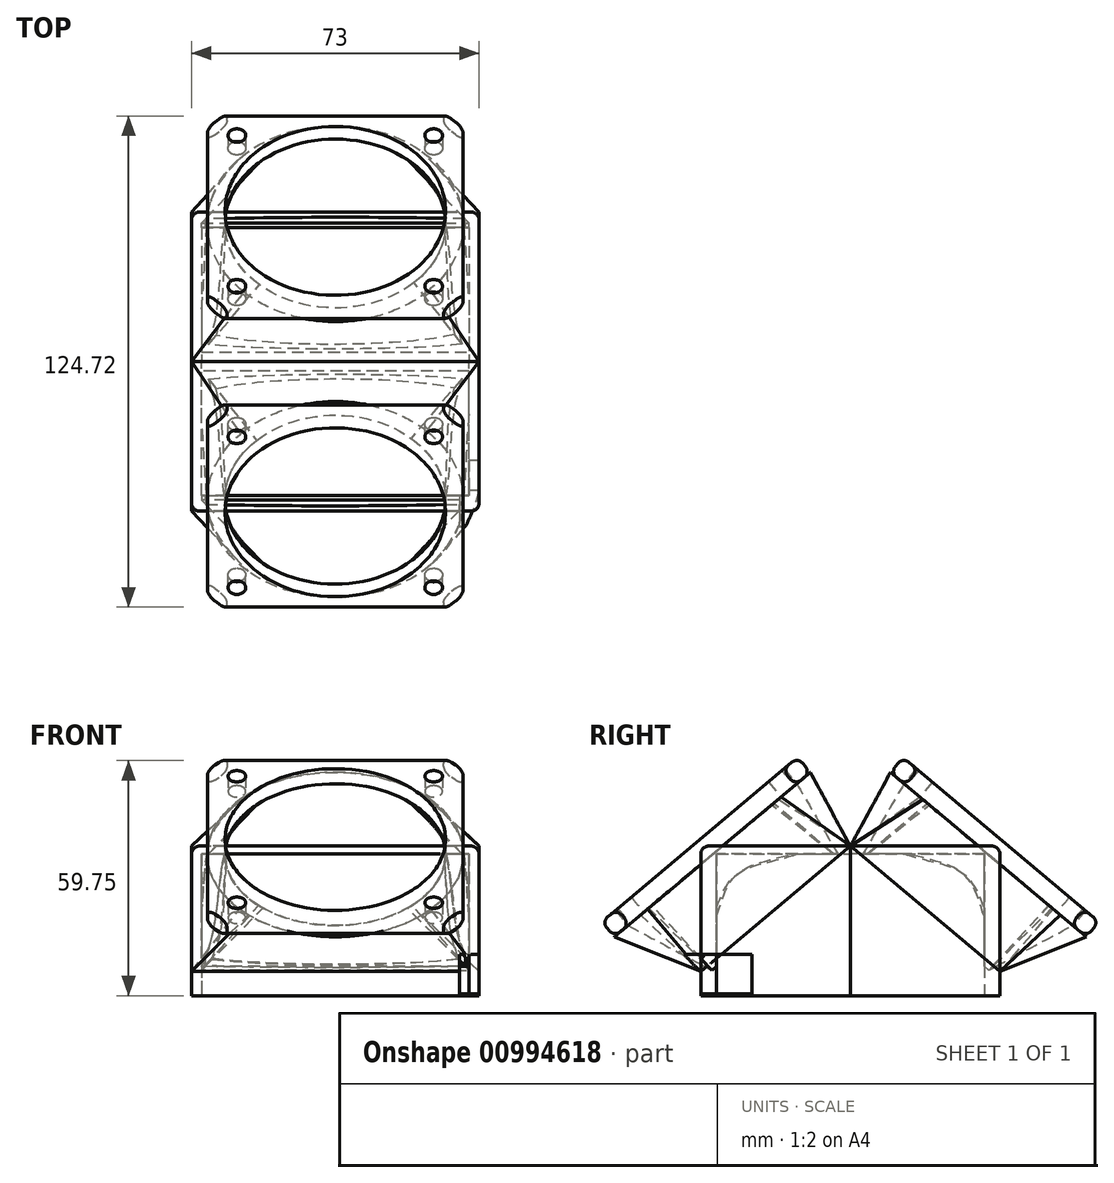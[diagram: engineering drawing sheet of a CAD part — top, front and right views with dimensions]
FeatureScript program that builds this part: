
annotation { "Feature Type Name" : "Feature", "Feature Type Description" : "" }
export const myFeature = defineFeature(function(context is Context, id is Id, definition is map)
    precondition{}
    {
        {
            var Q0;
            Q0=qCreatedBy(makeId("Front.planeOp"),FACE);
            var sketch = newSketch(context, id + "F0", { "sketchPlane" : qUnion([Q0])});
            skLineSegment(sketch, "E0.bottom", {"start": v(-34, 18) * mm, "end": v(34, 18) * mm});
            skLineSegment(sketch, "E0.top", {"start": v(-34, -18) * mm, "end": v(34, -18) * mm});
            skLineSegment(sketch, "E0.left", {"start": v(-34, 18) * mm, "end": v(-34, -18) * mm});
            skLineSegment(sketch, "E0.right", {"start": v(34, 18) * mm, "end": v(34, -18) * mm});
            skPoint(sketch, "E0.middle", {"position": v(0, 0) * mm});
            skSolve(sketch);
        }
        {
            var Q0;
            Q0=makeQuery(id+"F0.imprint","IMPRINT",FACE,{"disambiguationData":[TD([[makeQuery(id+"F0.imprint","IMPRINT",EDGE,{"derivedFrom":sQuery(id+"F0.wireOp",EDGE,"E0.bottom")}),-1.0]])]});
            extrude(context, id + "F1", {"entities" : qUnion([Q0]), "depth" : 34 * mm, "offsetDistance" : 25 * mm});
        }
        {
            var Q0;
            Q0=makeQuery(id+"F0.imprint","IMPRINT",FACE,{"disambiguationData":[TD([[makeQuery(id+"F0.imprint","IMPRINT",EDGE,{"derivedFrom":sQuery(id+"F0.wireOp",EDGE,"E0.bottom")}),-1.0]])]});
            var sketch = newSketch(context, id + "F2", { "sketchPlane" : qUnion([Q0])});
            skLineSegment(sketch, "E1", {"start": v(0, 18) * mm, "end": v(0, -18) * mm, "construction": true});
            skSolve(sketch);
        }
        {
            var Q0;
            Q0=sQuery(id+"F0.wireOp",EDGE,"E0.top");
            cPlane(context, id + "F3", {"entities" : qUnion([Q0]), "cplaneType" : CPlaneType.LINE_ANGLE, "offset" : 25 * mm, "angle" : 50 * degree, "oppositeDirection" : true, "width" : 150 * mm, "height" : 150 * mm});
        }
        {
            var Q0;
            Q0=sQuery(id+"F0.wireOp",EDGE,"E0.bottom");
            var Q1;
            Q1=qBodyType(qCreatedBy(id+"F5",EDGE),BodyType.WIRE);
            cPlane(context, id + "F4", {"entities" : qUnion([Q0, Q1]), "cplaneType" : CPlaneType.LINE_ANGLE, "offset" : 25 * mm, "angle" : 50 * degree, "oppositeDirection" : true, "width" : 150 * mm, "height" : 150 * mm});
        }
        {
            var Q0;
            Q0=qCreatedBy(id+"F4.planeOp",FACE);
            var sketch = newSketch(context, id + "F5", { "sketchPlane" : qUnion([Q0])});
            skLineSegment(sketch, "E2.bottom", {"start": v(34, -8.77) * mm, "end": v(-34, -8.77) * mm});
            skLineSegment(sketch, "E2.top", {"start": v(34, 34.4) * mm, "end": v(-34, 34.4) * mm});
            skLineSegment(sketch, "E2.left", {"start": v(34, -8.77) * mm, "end": v(34, 34.4) * mm});
            skLineSegment(sketch, "E2.right", {"start": v(-34, -8.77) * mm, "end": v(-34, 34.4) * mm});
            skSolve(sketch);
        }
        {
            var Q0;
            Q0=qCreatedBy(id+"F3.planeOp",FACE);
            cPlane(context, id + "F6", {"entities" : qUnion([Q0]), "cplaneType" : CPlaneType.OFFSET, "offset" : 50 * mm, "oppositeDirection" : true, "width" : 150 * mm, "height" : 150 * mm});
        }
        {
            var Q0;
            Q0=qCreatedBy(id+"F6.planeOp",FACE);
            var sketch = newSketch(context, id + "F7", { "sketchPlane" : qUnion([Q0])});
            skArc(sketch, "E3", {"start": v(19.5, 35.49) * mm, "mid": v(0.77, 43.38) * mm, "end": v(-18.36, 36.53) * mm});
            skArc(sketch, "E4", {"start": v(-18.36, 36.53) * mm, "mid": v(-27.98, 16.5) * mm, "end": v(-19.97, -4.24) * mm});
            skArc(sketch, "E5", {"start": v(-19.97, -4.24) * mm, "mid": v(-0.48, -12.6) * mm, "end": v(19.28, -4.91) * mm});
            skArc(sketch, "E6", {"start": v(19.28, -4.91) * mm, "mid": v(28, 15.24) * mm, "end": v(19.5, 35.49) * mm});
            skSolve(sketch);
        }
        {
            var Q0;
            Q0=qSketchRegion(id+"F5",true);
            var Q1;
            Q1=makeQuery(id+"F7.imprint","IMPRINT",FACE,{"disambiguationData":[TD([[makeQuery(id+"F7.imprint","IMPRINT",EDGE,{"derivedFrom":sQuery(id+"F7.wireOp",EDGE,"E3")}),1.0]])]});
            loft(context, id + "F8", {"sheetProfilesArray" : [{ "sheetProfileEntities" : qUnion([Q0]) }, { "sheetProfileEntities" : qUnion([Q1]) }]});
        }
        {
            var Q0;
            Q0=makeQuery(id+"F2.imprint","IMPRINT",FACE,{"disambiguationData":[TD([[makeQuery(id+"F2.imprint","IMPRINT",EDGE,{"derivedFrom":makeQuery(id+"F0.imprint","IMPRINT",EDGE,{"derivedFrom":sQuery(id+"F0.wireOp",EDGE,"E0.bottom")})}),-1.0]])]});
            var sketch = newSketch(context, id + "F9", { "sketchPlane" : qUnion([Q0])});
            skLineSegment(sketch, "E7.bottom", {"start": v(36.5, 20) * mm, "end": v(-36.5, 20) * mm});
            skLineSegment(sketch, "E7.top", {"start": v(36.5, -18) * mm, "end": v(-36.5, -18) * mm});
            skLineSegment(sketch, "E7.left", {"start": v(36.5, 20) * mm, "end": v(36.5, -18) * mm});
            skLineSegment(sketch, "E7.right", {"start": v(-36.5, 20) * mm, "end": v(-36.5, -18) * mm});
            skPoint(sketch, "E7.middle", {"position": v(0, 0) * mm});
            skSolve(sketch);
        }
        {
            var Q0;
            Q0=qSketchRegion(id+"F9",true);
            extrude(context, id + "F10", {"entities" : qUnion([Q0]), "depth" : 38 * mm, "offsetDistance" : 25 * mm});
        }
        {
            var Q0;
            Q0=sQuery(id+"F9.wireOp",EDGE,"E7.bottom");
            cPlane(context, id + "F11", {"entities" : qUnion([Q0]), "cplaneType" : CPlaneType.LINE_ANGLE, "offset" : 25 * mm, "angle" : 50 * degree, "width" : 150 * mm, "height" : 150 * mm});
        }
        {
            var Q0;
            Q0=qCreatedBy(id+"F11.planeOp",FACE);
            var sketch = newSketch(context, id + "F12", { "sketchPlane" : qUnion([Q0])});
            skLineSegment(sketch, "E8.bottom", {"start": v(-36.5, 12.86) * mm, "end": v(36.5, 12.86) * mm});
            skLineSegment(sketch, "E8.top", {"start": v(-36.5, -36.75) * mm, "end": v(36.5, -36.75) * mm});
            skLineSegment(sketch, "E8.left", {"start": v(-36.5, 12.86) * mm, "end": v(-36.5, -36.75) * mm});
            skLineSegment(sketch, "E8.right", {"start": v(36.5, 12.86) * mm, "end": v(36.5, -36.75) * mm});
            skSolve(sketch);
        }
        {
            var Q0;
            Q0=qCreatedBy(id+"F6.planeOp",FACE);
            var sketch = newSketch(context, id + "F13", { "sketchPlane" : qUnion([Q0])});
            skArc(sketch, "E9", {"start": v(-24.1, -6.4) * mm, "mid": v(-0.67, -17.1) * mm, "end": v(23.2, -7.38) * mm});
            skArc(sketch, "E10", {"start": v(-22.1, 39.22) * mm, "mid": v(-32.47, 16.82) * mm, "end": v(-24.1, -6.4) * mm});
            skArc(sketch, "E11", {"start": v(24.32, 36.95) * mm, "mid": v(1.59, 47.85) * mm, "end": v(-22.1, 39.22) * mm});
            skArc(sketch, "E12", {"start": v(23.2, -7.38) * mm, "mid": v(32.49, 14.56) * mm, "end": v(24.32, 36.95) * mm});
            skSolve(sketch);
        }
        {
            var Q0;
            Q0=qCreatedBy(id+"F6.planeOp",FACE);
            var sketch = newSketch(context, id + "F14", { "sketchPlane" : qUnion([Q0])});
            skLineSegment(sketch, "E13.bottom", {"start": v(-32.5, -17.1) * mm, "end": v(32.5, -17.1) * mm});
            skLineSegment(sketch, "E13.top", {"start": v(-32.5, 47.9) * mm, "end": v(32.5, 47.9) * mm});
            skLineSegment(sketch, "E13.left", {"start": v(-32.5, -17.1) * mm, "end": v(-32.5, 47.9) * mm});
            skLineSegment(sketch, "E13.right", {"start": v(32.5, -17.1) * mm, "end": v(32.5, 47.9) * mm});
            skPoint(sketch, "E13.middle", {"position": v(0, 15.4) * mm});
            skSolve(sketch);
        }
        {
            var Q0;
            Q0=qCreatedBy(id+"F6.planeOp",FACE);
            var sketch = newSketch(context, id + "F15", { "sketchPlane" : qUnion([Q0])});
            skLineSegment(sketch, "E14.bottom", {"start": v(-25, -9.6) * mm, "end": v(25, -9.6) * mm, "construction": true});
            skLineSegment(sketch, "E14.top", {"start": v(-25, 40.4) * mm, "end": v(25, 40.4) * mm, "construction": true});
            skLineSegment(sketch, "E14.left", {"start": v(-25, -9.6) * mm, "end": v(-25, 40.4) * mm, "construction": true});
            skLineSegment(sketch, "E14.right", {"start": v(25, -9.6) * mm, "end": v(25, 40.4) * mm, "construction": true});
            skPoint(sketch, "E14.middle", {"position": v(0, 15.4) * mm});
            skSolve(sketch);
        }
        {
            var Q0;
            Q0=qCreatedBy(id+"F6.planeOp",FACE);
            var sketch = newSketch(context, id + "F16", { "sketchPlane" : qUnion([Q0])});
            skCircle(sketch, "E15", {"center": v(25, -9.6) * mm, "radius": 2.25 * mm});
            skCircle(sketch, "E16", {"center": v(-25, -9.6) * mm, "radius": 2.25 * mm});
            skCircle(sketch, "E17", {"center": v(-25, 40.4) * mm, "radius": 2.25 * mm});
            skCircle(sketch, "E18", {"center": v(25, 40.4) * mm, "radius": 2.25 * mm});
            skSolve(sketch);
        }
        {
            var Q0;
            Q0=makeQuery(id+"F8.opLoft","CAP_FACE",FACE,{"disambiguationData":[OSD([makeQuery(id+"F7.imprint","IMPRINT",FACE,{"disambiguationData":[TD([[makeQuery(id+"F7.imprint","IMPRINT",EDGE,{"derivedFrom":sQuery(id+"F7.wireOp",EDGE,"E3")}),1.0]])]})])],"isStart":true});
            var Q1;
            Q1=makeQuery(id+"F16.imprint","IMPRINT",FACE,{"disambiguationData":[TD([[makeQuery(id+"F16.imprint","IMPRINT",EDGE,{"derivedFrom":sQuery(id+"F16.wireOp",EDGE,"E18")}),1.0]])]});
            var Q2;
            Q2=makeQuery(id+"F16.imprint","IMPRINT",FACE,{"disambiguationData":[TD([[makeQuery(id+"F16.imprint","IMPRINT",EDGE,{"derivedFrom":sQuery(id+"F16.wireOp",EDGE,"E17")}),1.0]])]});
            var Q3;
            Q3=makeQuery(id+"F16.imprint","IMPRINT",FACE,{"disambiguationData":[TD([[makeQuery(id+"F16.imprint","IMPRINT",EDGE,{"derivedFrom":sQuery(id+"F16.wireOp",EDGE,"E16")}),1.0]])]});
            var Q4;
            Q4=makeQuery(id+"F16.imprint","IMPRINT",FACE,{"disambiguationData":[TD([[makeQuery(id+"F16.imprint","IMPRINT",EDGE,{"derivedFrom":sQuery(id+"F16.wireOp",EDGE,"E15")}),1.0]])]});
            extrude(context, id + "F17", {"entities" : qUnion([Q0, Q1, Q2, Q3, Q4]), "depth" : 5 * mm, "offsetDistance" : 25 * mm});
        }
        {
            var Q0;
            Q0=makeQuery(id+"F12.imprint","IMPRINT",FACE,{"disambiguationData":[TD([[makeQuery(id+"F12.imprint","IMPRINT",EDGE,{"derivedFrom":sQuery(id+"F12.wireOp",EDGE,"E8.bottom")}),-1.0]])]});
            var Q1;
            Q1=qSketchRegion(id+"F13",true);
            loft(context, id + "F18", {"sheetProfilesArray" : [{ "sheetProfileEntities" : qUnion([Q0]) }, { "sheetProfileEntities" : qUnion([Q1]) }]});
        }
        {
            var Q0;
            Q0=makeQuery(id+"F14.imprint","IMPRINT",FACE,{"disambiguationData":[TD([[makeQuery(id+"F14.imprint","IMPRINT",EDGE,{"derivedFrom":sQuery(id+"F14.wireOp",EDGE,"E13.bottom")}),1.0]])]});
            extrude(context, id + "F19", {"entities" : qUnion([Q0]), "oppositeDirection" : true, "depth" : 5 * mm, "offsetDistance" : 25 * mm});
        }
        {
            var Q0;
            Q0=makeQuery(id+"F17.opExtrude","SWEPT_BODY",BODY,{"disambiguationData":[OSD([sQuery(id+"F16.wireOp",EDGE,"E18")])]});
            var Q1;
            Q1=makeQuery(id+"F17.opExtrude","SWEPT_BODY",BODY,{"disambiguationData":[OSD([sQuery(id+"F16.wireOp",EDGE,"E17")])]});
            var Q2;
            Q2=makeQuery(id+"F17.opExtrude","SWEPT_BODY",BODY,{"disambiguationData":[OSD([sQuery(id+"F16.wireOp",EDGE,"E16")])]});
            var Q3;
            Q3=makeQuery(id+"F17.opExtrude","SWEPT_BODY",BODY,{"disambiguationData":[OSD([sQuery(id+"F16.wireOp",EDGE,"E15")])]});
            var Q4;
            Q4=makeQuery(id+"F17.opExtrude","SWEPT_BODY",BODY,{"disambiguationData":[OSD([makeQuery(id+"F7.imprint","IMPRINT",FACE,{"disambiguationData":[TD([[makeQuery(id+"F7.imprint","IMPRINT",EDGE,{"derivedFrom":sQuery(id+"F7.wireOp",EDGE,"E3")}),1.0]])]})])]});
            var Q5;
            Q5=makeQuery(id+"F8.opLoft","SWEPT_BODY",BODY,{"disambiguationData":[OSD([makeQuery(id+"F5.imprint","IMPRINT",FACE,{"disambiguationData":[TD([[makeQuery(id+"F5.imprint","IMPRINT",EDGE,{"derivedFrom":sQuery(id+"F5.wireOp",EDGE,"sHmJ6Bm4-Lffu-TfJG-ELbj-xKBSEGzgKOYK.bottom")}),-1.0]])]}),makeQuery(id+"F7.imprint","IMPRINT",FACE,{"disambiguationData":[TD([[makeQuery(id+"F7.imprint","IMPRINT",EDGE,{"derivedFrom":sQuery(id+"F7.wireOp",EDGE,"E3")}),1.0]])]})])]});
            var Q6;
            Q6=makeQuery(id+"F1.opExtrude","SWEPT_BODY",BODY,{"disambiguationData":[OSD([sQuery(id+"F0.wireOp",EDGE,"E0.bottom"),sQuery(id+"F0.wireOp",EDGE,"E0.top"),sQuery(id+"F0.wireOp",EDGE,"E0.left"),sQuery(id+"F0.wireOp",EDGE,"E0.right")])]});
            var Q7;
            Q7=makeQuery(id+"F10.opExtrude","SWEPT_BODY",BODY,{"disambiguationData":[OSD([sQuery(id+"F9.wireOp",EDGE,"E7.bottom"),sQuery(id+"F9.wireOp",EDGE,"E7.top"),sQuery(id+"F9.wireOp",EDGE,"E7.left"),sQuery(id+"F9.wireOp",EDGE,"E7.right")])]});
            var Q8;
            Q8=makeQuery(id+"F18.opLoft","SWEPT_BODY",BODY,{"disambiguationData":[OSD([makeQuery(id+"F12.imprint","IMPRINT",FACE,{"disambiguationData":[TD([[makeQuery(id+"F12.imprint","IMPRINT",EDGE,{"derivedFrom":sQuery(id+"F12.wireOp",EDGE,"E8.bottom")}),-1.0]])]}),makeQuery(id+"F13.imprint","IMPRINT",FACE,{"disambiguationData":[TD([[makeQuery(id+"F13.imprint","IMPRINT",EDGE,{"derivedFrom":sQuery(id+"F13.wireOp",EDGE,"q23MTACi-eoCC-Vc5T-UU1i-hVDggLDGJppy")}),1.0]])]})])]});
            var Q9;
            Q9=makeQuery(id+"F19.opExtrude","SWEPT_BODY",BODY,{"disambiguationData":[OSD([sQuery(id+"F14.wireOp",EDGE,"E13.bottom"),sQuery(id+"F14.wireOp",EDGE,"E13.top"),sQuery(id+"F14.wireOp",EDGE,"E13.left"),sQuery(id+"F14.wireOp",EDGE,"E13.right")])]});
            booleanBodies(context, id + "F20", {"operationType" : BooleanOperationType.SUBTRACTION, "tools" : qUnion([Q0, Q1, Q2, Q3, Q4, Q5, Q6]), "targets" : qUnion([Q7, Q8, Q9])});
        }
        {
            var Q0;
            Q0=makeQuery(id+"F19.opExtrude","SWEPT_EDGE",EDGE,{"disambiguationData":[OSD([sQuery(id+"F14.wireOp",EDGE,"E13.top"),sQuery(id+"F14.wireOp",EDGE,"E13.right")])]});
            var Q1;
            Q1=makeQuery(id+"F19.opExtrude","SWEPT_EDGE",EDGE,{"disambiguationData":[OSD([sQuery(id+"F14.wireOp",EDGE,"E13.top"),sQuery(id+"F14.wireOp",EDGE,"E13.left")])]});
            var Q2;
            Q2=makeQuery(id+"F19.opExtrude","SWEPT_EDGE",EDGE,{"disambiguationData":[OSD([sQuery(id+"F14.wireOp",EDGE,"E13.bottom"),sQuery(id+"F14.wireOp",EDGE,"E13.right")])]});
            var Q3;
            Q3=makeQuery(id+"F19.opExtrude","SWEPT_EDGE",EDGE,{"disambiguationData":[OSD([sQuery(id+"F14.wireOp",EDGE,"E13.bottom"),sQuery(id+"F14.wireOp",EDGE,"E13.left")])]});
            chamfer(context, id + "F21", {"entities" : qUnion([Q0, Q1, Q2, Q3]), "width" : 5 * mm, "tangentPropagation" : true});
        }
        {
            var Q0;
            Q0=makeQuery(id+"F19.opExtrude","CAP_EDGE",EDGE,{"disambiguationData":[OSD([sQuery(id+"F14.wireOp",EDGE,"E13.left")])],"isStart":false});
            var Q1;
            Q1=makeQuery(id+"F19.opExtrude","CAP_EDGE",EDGE,{"disambiguationData":[OSD([sQuery(id+"F14.wireOp",EDGE,"E13.top")])],"isStart":false});
            var Q2;
            Q2=makeQuery(id+"F19.opExtrude","CAP_EDGE",EDGE,{"disambiguationData":[OSD([sQuery(id+"F14.wireOp",EDGE,"E13.right")])],"isStart":false});
            var Q3;
            Q3=makeQuery(id+"F19.opExtrude","CAP_EDGE",EDGE,{"disambiguationData":[OSD([sQuery(id+"F14.wireOp",EDGE,"E13.bottom")])],"isStart":false});
            var Q4;
            Q4=makeQuery(id+"F19.opExtrude","CAP_EDGE",EDGE,{"disambiguationData":[OSD([sQuery(id+"F14.wireOp",EDGE,"E13.left")])],"isStart":true});
            var Q5;
            Q5=makeQuery(id+"F19.opExtrude","CAP_EDGE",EDGE,{"disambiguationData":[OSD([sQuery(id+"F14.wireOp",EDGE,"E13.bottom")])],"isStart":true});
            var Q6;
            Q6=makeQuery(id+"F19.opExtrude","CAP_EDGE",EDGE,{"disambiguationData":[OSD([sQuery(id+"F14.wireOp",EDGE,"E13.right")])],"isStart":true});
            var Q7;
            Q7=makeQuery(id+"F19.opExtrude","CAP_EDGE",EDGE,{"disambiguationData":[OSD([sQuery(id+"F14.wireOp",EDGE,"E13.top")])],"isStart":true});
            var Q8;
            Q8=makeQuery(id+"F10.opExtrude","CAP_EDGE",EDGE,{"disambiguationData":[OSD([sQuery(id+"F9.wireOp",EDGE,"E7.right")])],"isStart":false});
            var Q9;
            {var subQ0=sQuery(id+"F9.wireOp",EDGE,"E7.bottom");var subQ1=sQuery(id+"F9.wireOp",EDGE,"E7.right");Q9=makeQuery(id+"F20.opBoolean","SPLIT",EDGE,{"disambiguationData":[TD([makeQuery(id+"F10.opExtrude","SWEPT_FACE",FACE,{"disambiguationData":[OSD([subQ1])]})])],"derivedFrom":makeQuery(id+"F10.opExtrude","CAP_EDGE",EDGE,{"disambiguationData":[OSD([subQ0])],"isStart":false})});}
            var Q10;
            Q10=makeQuery(id+"F10.opExtrude","SWEPT_EDGE",EDGE,{"disambiguationData":[OSD([sQuery(id+"F9.wireOp",EDGE,"E7.bottom"),sQuery(id+"F9.wireOp",EDGE,"E7.right")])]});
            var Q11;
            Q11=makeQuery(id+"F10.opExtrude","CAP_EDGE",EDGE,{"disambiguationData":[OSD([sQuery(id+"F9.wireOp",EDGE,"E7.left")])],"isStart":false});
            var Q12;
            Q12=makeQuery(id+"F10.opExtrude","SWEPT_EDGE",EDGE,{"disambiguationData":[OSD([sQuery(id+"F9.wireOp",EDGE,"E7.bottom"),sQuery(id+"F9.wireOp",EDGE,"E7.left")])]});
            var Q13;
            {var subQ0=sQuery(id+"F9.wireOp",EDGE,"E7.bottom");var subQ1=sQuery(id+"F9.wireOp",EDGE,"E7.left");Q13=makeQuery(id+"F20.opBoolean","SPLIT",EDGE,{"disambiguationData":[TD([makeQuery(id+"F10.opExtrude","SWEPT_FACE",FACE,{"disambiguationData":[OSD([subQ1])]})])],"derivedFrom":makeQuery(id+"F10.opExtrude","CAP_EDGE",EDGE,{"disambiguationData":[OSD([subQ0])],"isStart":false})});}
            fillet(context, id + "F22", {"entities" : qUnion([Q0, Q1, Q2, Q3, Q4, Q5, Q6, Q7, Q8, Q9, Q10, Q11, Q12, Q13]), "radius" : 2 * mm, "tangentPropagation" : true, "allowEdgeOverflow" : false});
        }
        {
            var Q0;
            Q0=makeQuery(id+"F10.opExtrude","SWEPT_BODY",BODY,{"disambiguationData":[OSD([sQuery(id+"F9.wireOp",EDGE,"E7.bottom"),sQuery(id+"F9.wireOp",EDGE,"E7.top"),sQuery(id+"F9.wireOp",EDGE,"E7.left"),sQuery(id+"F9.wireOp",EDGE,"E7.right")])]});
            var Q1;
            Q1=sQuery(id+"F2.wireOp",EDGE,"E1");
            transform(context, id + "F23", {"entities" : qUnion([Q0]), "transformType" : TransformType.ROTATION, "transformAxis" : qUnion([Q1]), "angle" : 180 * degree, "makeCopy" : true});
        }
        {
            var Q0;
            Q0=makeQuery(id+"F18.opLoft","SWEPT_BODY",BODY,{"disambiguationData":[OSD([makeQuery(id+"F12.imprint","IMPRINT",FACE,{"disambiguationData":[TD([[makeQuery(id+"F12.imprint","IMPRINT",EDGE,{"derivedFrom":sQuery(id+"F12.wireOp",EDGE,"E8.bottom")}),-1.0]])]}),makeQuery(id+"F13.imprint","IMPRINT",FACE,{"disambiguationData":[TD([[makeQuery(id+"F13.imprint","IMPRINT",EDGE,{"derivedFrom":sQuery(id+"F13.wireOp",EDGE,"q23MTACi-eoCC-Vc5T-UU1i-hVDggLDGJppy")}),1.0]])]})])]});
            var Q1;
            Q1=sQuery(id+"F2.wireOp",EDGE,"E1");
            transform(context, id + "F24", {"entities" : qUnion([Q0]), "transformType" : TransformType.ROTATION, "transformAxis" : qUnion([Q1]), "angle" : 180 * degree, "makeCopy" : true});
        }
        {
            var Q0;
            Q0=makeQuery(id+"F19.opExtrude","SWEPT_BODY",BODY,{"disambiguationData":[OSD([sQuery(id+"F14.wireOp",EDGE,"E13.bottom"),sQuery(id+"F14.wireOp",EDGE,"E13.top"),sQuery(id+"F14.wireOp",EDGE,"E13.left"),sQuery(id+"F14.wireOp",EDGE,"E13.right")])]});
            var Q1;
            Q1=sQuery(id+"F2.wireOp",EDGE,"E1");
            transform(context, id + "F25", {"entities" : qUnion([Q0]), "transformType" : TransformType.ROTATION, "transformAxis" : qUnion([Q1]), "angle" : 180 * degree, "makeCopy" : true});
        }
        {
            var Q0;
            Q0=makeQuery(id+"F10.opExtrude","SWEPT_FACE",FACE,{"disambiguationData":[OSD([sQuery(id+"F9.wireOp",EDGE,"E7.left")])]});
            var sketch = newSketch(context, id + "F26", { "sketchPlane" : qUnion([Q0])});
            skLineSegment(sketch, "E19.bottom", {"start": v(-25, -17.5) * mm, "end": v(-45, -17.5) * mm});
            skLineSegment(sketch, "E19.top", {"start": v(-25, -7.5) * mm, "end": v(-45, -7.5) * mm});
            skLineSegment(sketch, "E19.left", {"start": v(-25, -17.5) * mm, "end": v(-25, -7.5) * mm});
            skLineSegment(sketch, "E19.right", {"start": v(-45, -17.5) * mm, "end": v(-45, -7.5) * mm});
            skSolve(sketch);
        }
        {
            var Q0;
            Q0=qSketchRegion(id+"F26",true);
            extrude(context, id + "F27", {"entities" : qUnion([Q0]), "oppositeDirection" : true, "depth" : 5 * mm, "offsetDistance" : 25 * mm});
        }
        {
            var Q0;
            Q0=makeQuery(id+"F27.opExtrude","SWEPT_BODY",BODY,{"disambiguationData":[OSD([sQuery(id+"F26.wireOp",EDGE,"E19.bottom"),sQuery(id+"F26.wireOp",EDGE,"E19.top"),sQuery(id+"F26.wireOp",EDGE,"E19.left"),sQuery(id+"F26.wireOp",EDGE,"E19.right")])]});
            var Q1;
            Q1=makeQuery(id+"F10.opExtrude","SWEPT_BODY",BODY,{"disambiguationData":[OSD([sQuery(id+"F9.wireOp",EDGE,"E7.bottom"),sQuery(id+"F9.wireOp",EDGE,"E7.top"),sQuery(id+"F9.wireOp",EDGE,"E7.left"),sQuery(id+"F9.wireOp",EDGE,"E7.right")])]});
            var Q2;
            Q2=makeQuery(id+"F18.opLoft","SWEPT_BODY",BODY,{"disambiguationData":[OSD([makeQuery(id+"F12.imprint","IMPRINT",FACE,{"disambiguationData":[TD([[makeQuery(id+"F12.imprint","IMPRINT",EDGE,{"derivedFrom":sQuery(id+"F12.wireOp",EDGE,"E8.bottom")}),-1.0]])]}),makeQuery(id+"F13.imprint","IMPRINT",FACE,{"disambiguationData":[TD([[makeQuery(id+"F13.imprint","IMPRINT",EDGE,{"derivedFrom":sQuery(id+"F13.wireOp",EDGE,"q23MTACi-eoCC-Vc5T-UU1i-hVDggLDGJppy")}),1.0]])]})])]});
            booleanBodies(context, id + "F28", {"operationType" : BooleanOperationType.SUBTRACTION, "tools" : qUnion([Q0]), "targets" : qUnion([Q1, Q2])});
        }
    });
